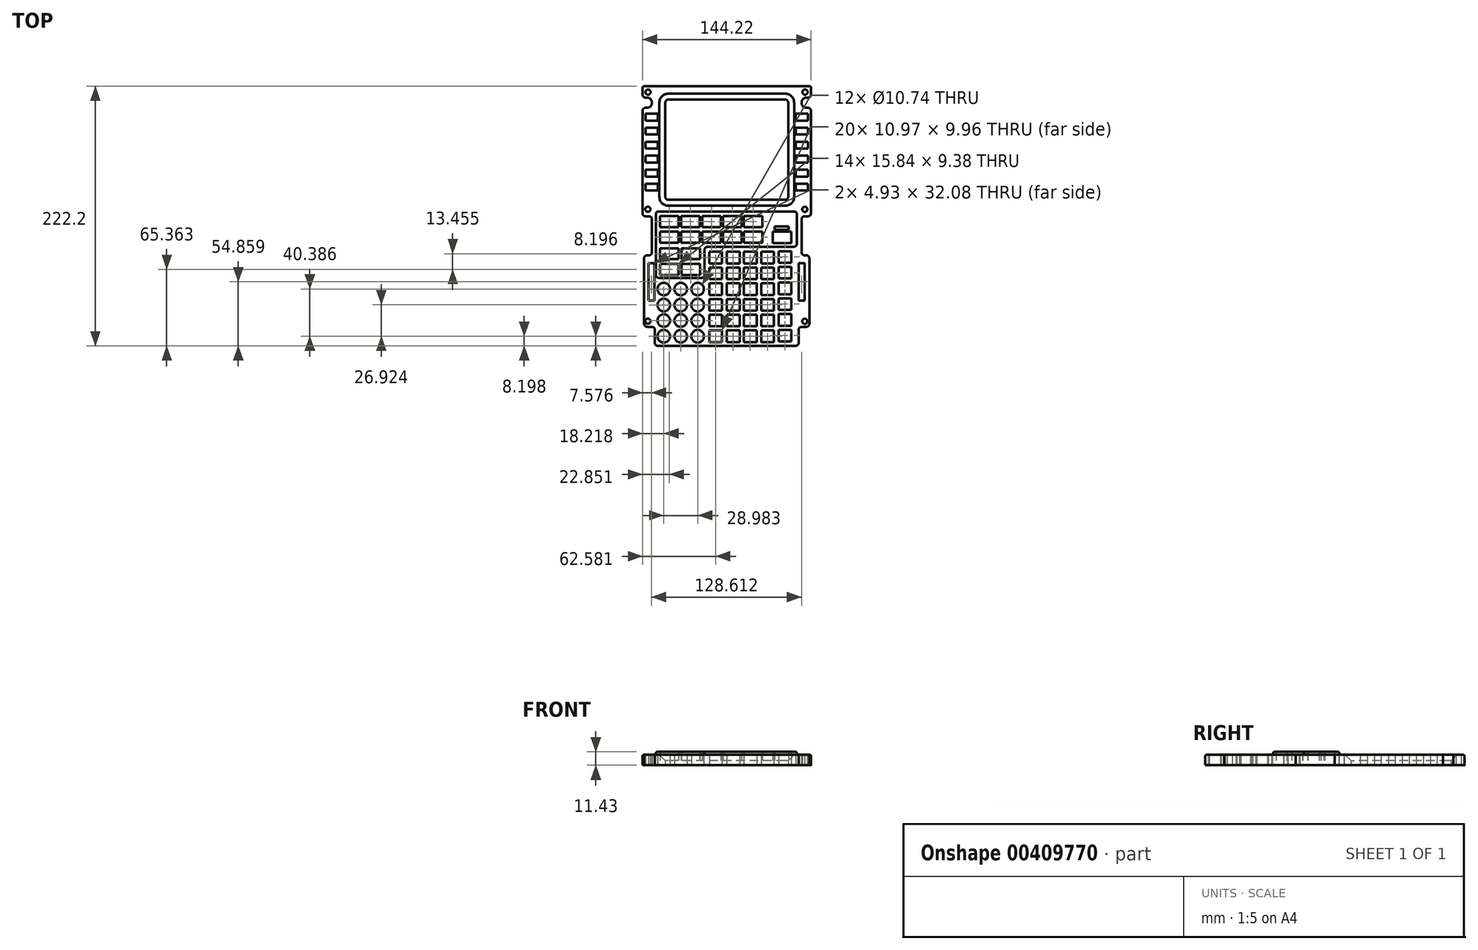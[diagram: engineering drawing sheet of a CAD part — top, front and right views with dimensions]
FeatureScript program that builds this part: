
annotation { "Feature Type Name" : "Feature", "Feature Type Description" : "" }
export const myFeature = defineFeature(function(context is Context, id is Id, definition is map)
    precondition{}
    {
        {
            var Q0;
            Q0=qCreatedBy(makeId("Top.planeOp"),FACE);
            var sketch = newSketch(context, id + "F0", { "sketchPlane" : qUnion([Q0])});
            skLineSegment(sketch, "E0.bottom", {"start": v(73.07, 113.67) * mm, "end": v(-73.07, 113.67) * mm});
            skLineSegment(sketch, "E0.top", {"start": v(73.07, -113.66) * mm, "end": v(-73.07, -113.66) * mm});
            skLineSegment(sketch, "E0.left", {"start": v(73.07, 113.67) * mm, "end": v(73.07, -113.66) * mm});
            skLineSegment(sketch, "E0.right", {"start": v(-73.07, 113.67) * mm, "end": v(-73.07, -113.66) * mm});
            skPoint(sketch, "E0.middle", {"position": v(0, 0) * mm});
            skLineSegment(sketch, "E1", {"start": v(0, 113.67) * mm, "end": v(0, 111.74) * mm});
            skLineSegment(sketch, "E2", {"start": v(-69.57, 102.01) * mm, "end": v(-68.34, 102.01) * mm});
            skLineSegment(sketch, "E3", {"start": v(-68.34, 93.24) * mm, "end": v(-69.57, 93.24) * mm});
            skLineSegment(sketch, "E4", {"start": v(-72.11, 90.7) * mm, "end": v(-72.11, 2.93) * mm});
            skLineSegment(sketch, "E5", {"start": v(-69.57, 0.4) * mm, "end": v(-66.53, 0.4) * mm});
            skLineSegment(sketch, "E6", {"start": v(-63.99, -2.15) * mm, "end": v(-63.99, -30.43) * mm});
            skLineSegment(sketch, "E7", {"start": v(-66.53, -32.97) * mm, "end": v(-68.15, -32.97) * mm});
            skLineSegment(sketch, "E8", {"start": v(-70.69, -35.51) * mm, "end": v(-70.69, -91.63) * mm});
            skLineSegment(sketch, "E9", {"start": v(-68.15, -94.17) * mm, "end": v(-64.1, -94.17) * mm});
            skLineSegment(sketch, "E10", {"start": v(-61.57, -96.71) * mm, "end": v(-61.57, -107.92) * mm});
            skLineSegment(sketch, "E11", {"start": v(-59.03, -110.46) * mm, "end": v(0, -110.46) * mm});
            skLineSegment(sketch, "E12", {"start": v(-72.11, 110.47) * mm, "end": v(-72.11, 108.94) * mm});
            skLineSegment(sketch, "E13", {"start": v(-70.84, 111.74) * mm, "end": v(-69.31, 111.74) * mm});
            skLineSegment(sketch, "E14", {"start": v(-72.11, 108.94) * mm, "end": v(-72.11, 104.55) * mm});
            skLineSegment(sketch, "E15", {"start": v(-69.31, 111.74) * mm, "end": v(0, 111.74) * mm});
            skPoint(sketch, "E16.visualSharp", {"position": v(-72.11, 111.74) * mm});
            skArc(sketch, "E16.filletArc", {"start": v(-70.84, 111.74) * mm, "mid": v(-71.74, 111.36) * mm, "end": v(-72.11, 110.47) * mm});
            skArc(sketch, "E17", {"start": v(-68.34, 93.24) * mm, "mid": v(-63.95, 97.62) * mm, "end": v(-68.34, 102.01) * mm});
            skPoint(sketch, "E18.visualSharp", {"position": v(-61.57, -110.46) * mm});
            skArc(sketch, "E18.filletArc", {"start": v(-61.57, -107.92) * mm, "mid": v(-60.82, -109.71) * mm, "end": v(-59.03, -110.46) * mm});
            skPoint(sketch, "E19.visualSharp", {"position": v(-61.57, -94.17) * mm});
            skArc(sketch, "E19.filletArc", {"start": v(-61.57, -96.71) * mm, "mid": v(-62.31, -94.92) * mm, "end": v(-64.1, -94.17) * mm});
            skPoint(sketch, "E20.visualSharp", {"position": v(-70.69, -94.17) * mm});
            skArc(sketch, "E20.filletArc", {"start": v(-70.69, -91.63) * mm, "mid": v(-69.94, -93.43) * mm, "end": v(-68.15, -94.17) * mm});
            skPoint(sketch, "E21.visualSharp", {"position": v(-70.69, -32.97) * mm});
            skArc(sketch, "E21.filletArc", {"start": v(-68.15, -32.97) * mm, "mid": v(-69.94, -33.72) * mm, "end": v(-70.69, -35.51) * mm});
            skPoint(sketch, "E22.visualSharp", {"position": v(-63.99, -32.97) * mm});
            skArc(sketch, "E22.filletArc", {"start": v(-66.53, -32.97) * mm, "mid": v(-64.73, -32.23) * mm, "end": v(-63.99, -30.43) * mm});
            skPoint(sketch, "E23.visualSharp", {"position": v(-63.99, 0.4) * mm});
            skArc(sketch, "E23.filletArc", {"start": v(-63.99, -2.15) * mm, "mid": v(-64.73, -0.35) * mm, "end": v(-66.53, 0.4) * mm});
            skPoint(sketch, "E24.visualSharp", {"position": v(-72.11, 0.4) * mm});
            skArc(sketch, "E24.filletArc", {"start": v(-72.11, 2.93) * mm, "mid": v(-71.37, 1.14) * mm, "end": v(-69.57, 0.4) * mm});
            skPoint(sketch, "E25.visualSharp", {"position": v(-72.11, 102.01) * mm});
            skArc(sketch, "E25.filletArc", {"start": v(-72.11, 104.55) * mm, "mid": v(-71.37, 102.76) * mm, "end": v(-69.57, 102.01) * mm});
            skPoint(sketch, "E26.visualSharp", {"position": v(-72.11, 93.24) * mm});
            skArc(sketch, "E26.filletArc", {"start": v(-69.57, 93.24) * mm, "mid": v(-71.37, 92.5) * mm, "end": v(-72.11, 90.7) * mm});
            skLineSegment(sketch, "E27.bottom", {"start": v(-59, 22.55) * mm, "end": v(-69.41, 22.55) * mm});
            skLineSegment(sketch, "E27.top", {"start": v(-59, 28.39) * mm, "end": v(-69.41, 28.39) * mm});
            skLineSegment(sketch, "E27.left", {"start": v(-59, 22.55) * mm, "end": v(-59, 28.39) * mm});
            skLineSegment(sketch, "E27.right", {"start": v(-69.41, 22.55) * mm, "end": v(-69.41, 28.39) * mm});
            skPoint(sketch, "E27.middle", {"position": v(-64.2, 25.47) * mm});
            skLineSegment(sketch, "E28.bottom", {"start": v(-59, 34.4) * mm, "end": v(-69.41, 34.4) * mm});
            skLineSegment(sketch, "E28.top", {"start": v(-59, 40.25) * mm, "end": v(-69.41, 40.25) * mm});
            skLineSegment(sketch, "E28.left", {"start": v(-59, 34.4) * mm, "end": v(-59, 40.25) * mm});
            skLineSegment(sketch, "E28.right", {"start": v(-69.41, 34.4) * mm, "end": v(-69.41, 40.25) * mm});
            skPoint(sketch, "E28.middle", {"position": v(-64.2, 37.33) * mm});
            skLineSegment(sketch, "E29.bottom", {"start": v(-59, 46.4) * mm, "end": v(-69.41, 46.4) * mm});
            skLineSegment(sketch, "E29.top", {"start": v(-59, 52.23) * mm, "end": v(-69.41, 52.23) * mm});
            skLineSegment(sketch, "E29.left", {"start": v(-59, 46.4) * mm, "end": v(-59, 52.23) * mm});
            skLineSegment(sketch, "E29.right", {"start": v(-69.41, 46.4) * mm, "end": v(-69.41, 52.23) * mm});
            skPoint(sketch, "E29.middle", {"position": v(-64.2, 49.31) * mm});
            skLineSegment(sketch, "E30.bottom", {"start": v(-59, 58.39) * mm, "end": v(-69.42, 58.39) * mm});
            skLineSegment(sketch, "E30.top", {"start": v(-59, 64.26) * mm, "end": v(-69.42, 64.26) * mm});
            skLineSegment(sketch, "E30.left", {"start": v(-59, 58.39) * mm, "end": v(-59, 64.26) * mm});
            skLineSegment(sketch, "E30.right", {"start": v(-69.42, 58.39) * mm, "end": v(-69.42, 64.26) * mm});
            skPoint(sketch, "E30.middle", {"position": v(-64.2, 61.32) * mm});
            skLineSegment(sketch, "E31.bottom", {"start": v(-59, 70.4) * mm, "end": v(-69.42, 70.4) * mm});
            skLineSegment(sketch, "E31.top", {"start": v(-59, 76.26) * mm, "end": v(-69.42, 76.26) * mm});
            skLineSegment(sketch, "E31.left", {"start": v(-59, 70.4) * mm, "end": v(-59, 76.26) * mm});
            skLineSegment(sketch, "E31.right", {"start": v(-69.42, 70.4) * mm, "end": v(-69.42, 76.26) * mm});
            skPoint(sketch, "E31.middle", {"position": v(-64.2, 73.33) * mm});
            skLineSegment(sketch, "E32.bottom", {"start": v(-59, 82.37) * mm, "end": v(-69.42, 82.37) * mm});
            skLineSegment(sketch, "E32.top", {"start": v(-59, 88.2) * mm, "end": v(-69.42, 88.2) * mm});
            skLineSegment(sketch, "E32.left", {"start": v(-59, 82.37) * mm, "end": v(-59, 88.2) * mm});
            skLineSegment(sketch, "E32.right", {"start": v(-69.42, 82.37) * mm, "end": v(-69.42, 88.2) * mm});
            skPoint(sketch, "E32.middle", {"position": v(-64.2, 85.29) * mm});
            skLineSegment(sketch, "E33", {"start": v(0, 100.27) * mm, "end": v(-50.04, 100.27) * mm});
            skLineSegment(sketch, "E34", {"start": v(-52.58, 97.73) * mm, "end": v(-52.58, 17.05) * mm});
            skLineSegment(sketch, "E35", {"start": v(-50.04, 14.51) * mm, "end": v(0, 14.51) * mm});
            skPoint(sketch, "E36.visualSharp", {"position": v(-52.58, 14.51) * mm});
            skArc(sketch, "E36.filletArc", {"start": v(-52.58, 17.05) * mm, "mid": v(-51.83, 15.26) * mm, "end": v(-50.04, 14.51) * mm});
            skPoint(sketch, "E37.visualSharp", {"position": v(-52.58, 100.27) * mm});
            skArc(sketch, "E37.filletArc", {"start": v(-50.04, 100.27) * mm, "mid": v(-51.83, 99.53) * mm, "end": v(-52.58, 97.73) * mm});
            skLineSegment(sketch, "E38", {"start": v(0, 105.03) * mm, "end": v(-54.96, 105.03) * mm});
            skLineSegment(sketch, "E39", {"start": v(-57.5, 102.49) * mm, "end": v(-57.5, 11.14) * mm});
            skLineSegment(sketch, "E40", {"start": v(-54.96, 8.6) * mm, "end": v(0, 8.6) * mm});
            skLineSegment(sketch, "E41.MirrorCS", {"start": v(59.03, -110.46) * mm, "end": v(0, -110.46) * mm});
            skArc(sketch, "E42.MirrorCS", {"start": v(61.57, -107.92) * mm, "mid": v(60.82, -109.71) * mm, "end": v(59.03, -110.46) * mm});
            skLineSegment(sketch, "E43.MirrorCS", {"start": v(61.57, -96.71) * mm, "end": v(61.57, -107.92) * mm});
            skArc(sketch, "E44.MirrorCS", {"start": v(61.57, -96.71) * mm, "mid": v(62.31, -94.92) * mm, "end": v(64.1, -94.17) * mm});
            skLineSegment(sketch, "E45.MirrorCS", {"start": v(68.15, -94.17) * mm, "end": v(64.1, -94.17) * mm});
            skArc(sketch, "E46.MirrorCS", {"start": v(70.69, -91.63) * mm, "mid": v(69.94, -93.43) * mm, "end": v(68.15, -94.17) * mm});
            skLineSegment(sketch, "E47.MirrorCS", {"start": v(70.69, -35.51) * mm, "end": v(70.69, -91.63) * mm});
            skArc(sketch, "E48.MirrorCS", {"start": v(68.15, -32.97) * mm, "mid": v(69.94, -33.72) * mm, "end": v(70.69, -35.51) * mm});
            skLineSegment(sketch, "E49.MirrorCS", {"start": v(66.53, -32.97) * mm, "end": v(68.15, -32.97) * mm});
            skArc(sketch, "E50.MirrorCS", {"start": v(66.53, -32.97) * mm, "mid": v(64.73, -32.23) * mm, "end": v(63.99, -30.43) * mm});
            skLineSegment(sketch, "E51.MirrorCS", {"start": v(63.99, -2.15) * mm, "end": v(63.99, -30.43) * mm});
            skArc(sketch, "E52.MirrorCS", {"start": v(63.99, -2.15) * mm, "mid": v(64.73, -0.35) * mm, "end": v(66.53, 0.4) * mm});
            skLineSegment(sketch, "E53.MirrorCS", {"start": v(69.57, 0.4) * mm, "end": v(66.53, 0.4) * mm});
            skArc(sketch, "E54.MirrorCS", {"start": v(72.11, 2.93) * mm, "mid": v(71.37, 1.14) * mm, "end": v(69.57, 0.4) * mm});
            skLineSegment(sketch, "E55.MirrorCS", {"start": v(72.11, 90.7) * mm, "end": v(72.11, 2.93) * mm});
            skLineSegment(sketch, "E56.MirrorCS", {"start": v(69.41, 22.55) * mm, "end": v(69.41, 28.39) * mm});
            skLineSegment(sketch, "E57.MirrorCS", {"start": v(59, 22.55) * mm, "end": v(69.41, 22.55) * mm});
            skLineSegment(sketch, "E58.MirrorCS", {"start": v(59, 22.55) * mm, "end": v(59, 28.39) * mm});
            skLineSegment(sketch, "E59.MirrorCS", {"start": v(59, 28.39) * mm, "end": v(69.41, 28.39) * mm});
            skLineSegment(sketch, "E60.MirrorCS", {"start": v(59, 34.4) * mm, "end": v(69.41, 34.4) * mm});
            skLineSegment(sketch, "E61.MirrorCS", {"start": v(59, 34.4) * mm, "end": v(59, 40.25) * mm});
            skLineSegment(sketch, "E62.MirrorCS", {"start": v(59, 40.25) * mm, "end": v(69.41, 40.25) * mm});
            skLineSegment(sketch, "E63.MirrorCS", {"start": v(69.41, 34.4) * mm, "end": v(69.41, 40.25) * mm});
            skLineSegment(sketch, "E64.MirrorCS", {"start": v(59, 46.4) * mm, "end": v(69.41, 46.4) * mm});
            skLineSegment(sketch, "E65.MirrorCS", {"start": v(59, 46.4) * mm, "end": v(59, 52.23) * mm});
            skLineSegment(sketch, "E66.MirrorCS", {"start": v(59, 52.23) * mm, "end": v(69.41, 52.23) * mm});
            skLineSegment(sketch, "E67.MirrorCS", {"start": v(69.41, 46.4) * mm, "end": v(69.41, 52.23) * mm});
            skLineSegment(sketch, "E68.MirrorCS", {"start": v(59, 58.39) * mm, "end": v(69.42, 58.39) * mm});
            skLineSegment(sketch, "E69.MirrorCS", {"start": v(69.42, 58.39) * mm, "end": v(69.42, 64.26) * mm});
            skLineSegment(sketch, "E70.MirrorCS", {"start": v(59, 64.26) * mm, "end": v(69.42, 64.26) * mm});
            skLineSegment(sketch, "E71.MirrorCS", {"start": v(59, 58.39) * mm, "end": v(59, 64.26) * mm});
            skLineSegment(sketch, "E72.MirrorCS", {"start": v(59, 70.4) * mm, "end": v(69.42, 70.4) * mm});
            skLineSegment(sketch, "E73.MirrorCS", {"start": v(69.42, 70.4) * mm, "end": v(69.42, 76.26) * mm});
            skLineSegment(sketch, "E74.MirrorCS", {"start": v(59, 76.26) * mm, "end": v(69.42, 76.26) * mm});
            skLineSegment(sketch, "E75.MirrorCS", {"start": v(59, 70.4) * mm, "end": v(59, 76.26) * mm});
            skLineSegment(sketch, "E76.MirrorCS", {"start": v(59, 82.37) * mm, "end": v(69.42, 82.37) * mm});
            skLineSegment(sketch, "E77.MirrorCS", {"start": v(69.42, 82.37) * mm, "end": v(69.42, 88.2) * mm});
            skLineSegment(sketch, "E78.MirrorCS", {"start": v(59, 88.2) * mm, "end": v(69.42, 88.2) * mm});
            skLineSegment(sketch, "E79.MirrorCS", {"start": v(59, 82.37) * mm, "end": v(59, 88.2) * mm});
            skArc(sketch, "E80.MirrorCS", {"start": v(69.57, 93.24) * mm, "mid": v(71.37, 92.5) * mm, "end": v(72.11, 90.7) * mm});
            skLineSegment(sketch, "E81.MirrorCS", {"start": v(68.34, 93.24) * mm, "end": v(69.57, 93.24) * mm});
            skArc(sketch, "E82.MirrorCS", {"start": v(68.34, 93.24) * mm, "mid": v(63.95, 97.62) * mm, "end": v(68.34, 102.01) * mm});
            skLineSegment(sketch, "E83.MirrorCS", {"start": v(69.57, 102.01) * mm, "end": v(68.34, 102.01) * mm});
            skArc(sketch, "E84.MirrorCS", {"start": v(72.11, 104.55) * mm, "mid": v(71.37, 102.76) * mm, "end": v(69.57, 102.01) * mm});
            skLineSegment(sketch, "E85.MirrorCS", {"start": v(72.11, 108.94) * mm, "end": v(72.11, 104.55) * mm});
            skLineSegment(sketch, "E86.MirrorCS", {"start": v(72.11, 110.47) * mm, "end": v(72.11, 108.94) * mm});
            skArc(sketch, "E87.MirrorCS", {"start": v(70.84, 111.74) * mm, "mid": v(71.74, 111.36) * mm, "end": v(72.11, 110.47) * mm});
            skLineSegment(sketch, "E88.MirrorCS", {"start": v(70.84, 111.74) * mm, "end": v(69.31, 111.74) * mm});
            skLineSegment(sketch, "E89.MirrorCS", {"start": v(69.31, 111.74) * mm, "end": v(0, 111.74) * mm});
            skLineSegment(sketch, "E90.MirrorCS", {"start": v(50.04, 14.51) * mm, "end": v(0, 14.51) * mm});
            skArc(sketch, "E91.MirrorCS", {"start": v(52.58, 17.05) * mm, "mid": v(51.83, 15.26) * mm, "end": v(50.04, 14.51) * mm});
            skLineSegment(sketch, "E92.MirrorCS", {"start": v(52.58, 97.73) * mm, "end": v(52.58, 17.05) * mm});
            skArc(sketch, "E93.MirrorCS", {"start": v(50.04, 100.27) * mm, "mid": v(51.83, 99.53) * mm, "end": v(52.58, 97.73) * mm});
            skLineSegment(sketch, "E94.MirrorCS", {"start": v(0, 100.27) * mm, "end": v(50.04, 100.27) * mm});
            skPoint(sketch, "E95.visualSharp", {"position": v(-57.5, 105.03) * mm});
            skArc(sketch, "E95.filletArc", {"start": v(-54.96, 105.03) * mm, "mid": v(-56.76, 104.28) * mm, "end": v(-57.5, 102.49) * mm});
            skPoint(sketch, "E96.visualSharp", {"position": v(-57.5, 8.6) * mm});
            skArc(sketch, "E96.filletArc", {"start": v(-57.5, 11.14) * mm, "mid": v(-56.76, 9.35) * mm, "end": v(-54.96, 8.6) * mm});
            skLineSegment(sketch, "E97.MirrorCS", {"start": v(54.96, 8.6) * mm, "end": v(0, 8.6) * mm});
            skArc(sketch, "E98.MirrorCS", {"start": v(57.5, 11.14) * mm, "mid": v(56.76, 9.35) * mm, "end": v(54.96, 8.6) * mm});
            skLineSegment(sketch, "E99.MirrorCS", {"start": v(57.5, 102.49) * mm, "end": v(57.5, 11.14) * mm});
            skArc(sketch, "E100.MirrorCS", {"start": v(54.96, 105.03) * mm, "mid": v(56.76, 104.28) * mm, "end": v(57.5, 102.49) * mm});
            skLineSegment(sketch, "E101.MirrorCS", {"start": v(0, 105.03) * mm, "end": v(54.96, 105.03) * mm});
            skCircle(sketch, "E102", {"center": v(-53.9, -61.88) * mm, "radius": 5.37 * mm});
            skCircle(sketch, "E103", {"center": v(-39.39, -61.88) * mm, "radius": 5.37 * mm});
            skCircle(sketch, "E104", {"center": v(-24.9, -61.88) * mm, "radius": 5.37 * mm});
            skCircle(sketch, "E105", {"center": v(-53.9, -75.58) * mm, "radius": 5.37 * mm});
            skCircle(sketch, "E106", {"center": v(-39.39, -75.58) * mm, "radius": 5.37 * mm});
            skCircle(sketch, "E107", {"center": v(-24.9, -75.58) * mm, "radius": 5.37 * mm});
            skCircle(sketch, "E108", {"center": v(-39.39, -88.8) * mm, "radius": 5.37 * mm});
            skCircle(sketch, "E109", {"center": v(-53.9, -88.8) * mm, "radius": 5.37 * mm});
            skCircle(sketch, "E110", {"center": v(-24.9, -88.8) * mm, "radius": 5.37 * mm});
            skCircle(sketch, "E111", {"center": v(-39.39, -102.26) * mm, "radius": 5.37 * mm});
            skCircle(sketch, "E112", {"center": v(-24.9, -102.26) * mm, "radius": 5.37 * mm});
            skCircle(sketch, "E113", {"center": v(-53.9, -102.26) * mm, "radius": 5.37 * mm});
            skLineSegment(sketch, "E114.bottom", {"start": v(-4.04, -29.98) * mm, "end": v(-15.02, -29.98) * mm});
            skLineSegment(sketch, "E114.top", {"start": v(-4.04, -39.93) * mm, "end": v(-15.02, -39.93) * mm});
            skLineSegment(sketch, "E114.left", {"start": v(-4.04, -29.98) * mm, "end": v(-4.04, -39.93) * mm});
            skLineSegment(sketch, "E114.right", {"start": v(-15.02, -29.98) * mm, "end": v(-15.02, -39.93) * mm});
            skPoint(sketch, "E114.middle", {"position": v(-9.53, -34.95) * mm});
            skLineSegment(sketch, "E115.bottom", {"start": v(-4.04, -43.44) * mm, "end": v(-15.02, -43.44) * mm});
            skLineSegment(sketch, "E115.top", {"start": v(-4.04, -53.4) * mm, "end": v(-15.02, -53.4) * mm});
            skLineSegment(sketch, "E115.left", {"start": v(-4.04, -43.44) * mm, "end": v(-4.04, -53.4) * mm});
            skLineSegment(sketch, "E115.right", {"start": v(-15.02, -43.44) * mm, "end": v(-15.02, -53.4) * mm});
            skPoint(sketch, "E115.middle", {"position": v(-9.53, -48.42) * mm});
            skLineSegment(sketch, "E116.bottom", {"start": v(-4.04, -66.85) * mm, "end": v(-15.02, -66.85) * mm});
            skLineSegment(sketch, "E116.top", {"start": v(-4.04, -56.9) * mm, "end": v(-15.02, -56.9) * mm});
            skLineSegment(sketch, "E116.left", {"start": v(-4.04, -66.85) * mm, "end": v(-4.04, -56.9) * mm});
            skLineSegment(sketch, "E116.right", {"start": v(-15.02, -66.85) * mm, "end": v(-15.02, -56.9) * mm});
            skPoint(sketch, "E116.middle", {"position": v(-9.53, -61.88) * mm});
            skLineSegment(sketch, "E117.bottom", {"start": v(-4.04, -80.32) * mm, "end": v(-15.02, -80.32) * mm});
            skLineSegment(sketch, "E117.top", {"start": v(-4.04, -70.36) * mm, "end": v(-15.02, -70.36) * mm});
            skLineSegment(sketch, "E117.left", {"start": v(-4.04, -80.32) * mm, "end": v(-4.04, -70.36) * mm});
            skLineSegment(sketch, "E117.right", {"start": v(-15.02, -80.32) * mm, "end": v(-15.02, -70.36) * mm});
            skPoint(sketch, "E117.middle", {"position": v(-9.53, -75.34) * mm});
            skLineSegment(sketch, "E118.bottom", {"start": v(-4.04, -93.79) * mm, "end": v(-15.02, -93.79) * mm});
            skLineSegment(sketch, "E118.top", {"start": v(-4.04, -83.82) * mm, "end": v(-15.02, -83.82) * mm});
            skLineSegment(sketch, "E118.left", {"start": v(-4.04, -93.79) * mm, "end": v(-4.04, -83.82) * mm});
            skLineSegment(sketch, "E118.right", {"start": v(-15.02, -93.79) * mm, "end": v(-15.02, -83.82) * mm});
            skPoint(sketch, "E118.middle", {"position": v(-9.53, -88.8) * mm});
            skLineSegment(sketch, "E119.bottom", {"start": v(-4.04, -97.28) * mm, "end": v(-15.02, -97.28) * mm});
            skLineSegment(sketch, "E119.top", {"start": v(-4.04, -107.24) * mm, "end": v(-15.02, -107.24) * mm});
            skLineSegment(sketch, "E119.left", {"start": v(-4.04, -97.28) * mm, "end": v(-4.04, -107.24) * mm});
            skLineSegment(sketch, "E119.right", {"start": v(-15.02, -97.28) * mm, "end": v(-15.02, -107.24) * mm});
            skPoint(sketch, "E119.middle", {"position": v(-9.53, -102.26) * mm});
            skLineSegment(sketch, "E120.bottom", {"start": v(10.97, -29.98) * mm, "end": v(0, -29.98) * mm});
            skLineSegment(sketch, "E120.top", {"start": v(10.97, -39.93) * mm, "end": v(0, -39.93) * mm});
            skLineSegment(sketch, "E120.left", {"start": v(10.97, -29.98) * mm, "end": v(10.97, -39.93) * mm});
            skLineSegment(sketch, "E120.right", {"start": v(0, -29.98) * mm, "end": v(0, -39.93) * mm});
            skLineSegment(sketch, "E121.bottom", {"start": v(10.97, -43.44) * mm, "end": v(0, -43.44) * mm});
            skLineSegment(sketch, "E121.top", {"start": v(10.97, -53.4) * mm, "end": v(0, -53.4) * mm});
            skLineSegment(sketch, "E121.left", {"start": v(10.97, -43.44) * mm, "end": v(10.97, -53.4) * mm});
            skLineSegment(sketch, "E121.right", {"start": v(0, -43.44) * mm, "end": v(0, -53.4) * mm});
            skLineSegment(sketch, "E122.bottom", {"start": v(10.97, -66.85) * mm, "end": v(0, -66.85) * mm});
            skLineSegment(sketch, "E122.top", {"start": v(10.97, -56.9) * mm, "end": v(0, -56.9) * mm});
            skLineSegment(sketch, "E122.left", {"start": v(10.97, -66.85) * mm, "end": v(10.97, -56.9) * mm});
            skLineSegment(sketch, "E122.right", {"start": v(0, -66.85) * mm, "end": v(0, -56.9) * mm});
            skLineSegment(sketch, "E123.bottom", {"start": v(10.97, -80.32) * mm, "end": v(0, -80.32) * mm});
            skLineSegment(sketch, "E123.top", {"start": v(10.97, -70.36) * mm, "end": v(0, -70.36) * mm});
            skLineSegment(sketch, "E123.left", {"start": v(10.97, -80.32) * mm, "end": v(10.97, -70.36) * mm});
            skLineSegment(sketch, "E123.right", {"start": v(0, -80.32) * mm, "end": v(0, -70.36) * mm});
            skLineSegment(sketch, "E124.bottom", {"start": v(10.97, -93.79) * mm, "end": v(0, -93.79) * mm});
            skLineSegment(sketch, "E124.top", {"start": v(10.97, -83.82) * mm, "end": v(0, -83.82) * mm});
            skLineSegment(sketch, "E124.left", {"start": v(10.97, -93.79) * mm, "end": v(10.97, -83.82) * mm});
            skLineSegment(sketch, "E124.right", {"start": v(0, -93.79) * mm, "end": v(0, -83.82) * mm});
            skLineSegment(sketch, "E125.bottom", {"start": v(10.97, -97.28) * mm, "end": v(0, -97.28) * mm});
            skLineSegment(sketch, "E125.top", {"start": v(10.97, -107.24) * mm, "end": v(0, -107.24) * mm});
            skLineSegment(sketch, "E125.left", {"start": v(10.97, -97.28) * mm, "end": v(10.97, -107.24) * mm});
            skLineSegment(sketch, "E125.right", {"start": v(0, -97.28) * mm, "end": v(0, -107.24) * mm});
            skLineSegment(sketch, "E126.bottom", {"start": v(25.63, -29.98) * mm, "end": v(14.65, -29.98) * mm});
            skLineSegment(sketch, "E126.top", {"start": v(25.63, -39.93) * mm, "end": v(14.65, -39.93) * mm});
            skLineSegment(sketch, "E126.left", {"start": v(25.63, -29.98) * mm, "end": v(25.63, -39.93) * mm});
            skLineSegment(sketch, "E126.right", {"start": v(14.65, -29.98) * mm, "end": v(14.65, -39.93) * mm});
            skLineSegment(sketch, "E127.bottom", {"start": v(25.63, -43.44) * mm, "end": v(14.65, -43.44) * mm});
            skLineSegment(sketch, "E127.top", {"start": v(25.63, -53.4) * mm, "end": v(14.65, -53.4) * mm});
            skLineSegment(sketch, "E127.left", {"start": v(25.63, -43.44) * mm, "end": v(25.63, -53.4) * mm});
            skLineSegment(sketch, "E127.right", {"start": v(14.65, -43.44) * mm, "end": v(14.65, -53.4) * mm});
            skLineSegment(sketch, "E128.bottom", {"start": v(25.63, -66.85) * mm, "end": v(14.65, -66.85) * mm});
            skLineSegment(sketch, "E128.top", {"start": v(25.63, -56.9) * mm, "end": v(14.65, -56.9) * mm});
            skLineSegment(sketch, "E128.left", {"start": v(25.63, -66.85) * mm, "end": v(25.63, -56.9) * mm});
            skLineSegment(sketch, "E128.right", {"start": v(14.65, -66.85) * mm, "end": v(14.65, -56.9) * mm});
            skLineSegment(sketch, "E129.bottom", {"start": v(25.63, -80.32) * mm, "end": v(14.65, -80.32) * mm});
            skLineSegment(sketch, "E129.top", {"start": v(25.63, -70.36) * mm, "end": v(14.65, -70.36) * mm});
            skLineSegment(sketch, "E129.left", {"start": v(25.63, -80.32) * mm, "end": v(25.63, -70.36) * mm});
            skLineSegment(sketch, "E129.right", {"start": v(14.65, -80.32) * mm, "end": v(14.65, -70.36) * mm});
            skLineSegment(sketch, "E130.bottom", {"start": v(25.63, -93.79) * mm, "end": v(14.65, -93.79) * mm});
            skLineSegment(sketch, "E130.top", {"start": v(25.63, -83.82) * mm, "end": v(14.65, -83.82) * mm});
            skLineSegment(sketch, "E130.left", {"start": v(25.63, -93.79) * mm, "end": v(25.63, -83.82) * mm});
            skLineSegment(sketch, "E130.right", {"start": v(14.65, -93.79) * mm, "end": v(14.65, -83.82) * mm});
            skLineSegment(sketch, "E131.bottom", {"start": v(25.63, -97.28) * mm, "end": v(14.65, -97.28) * mm});
            skLineSegment(sketch, "E131.top", {"start": v(25.63, -107.24) * mm, "end": v(14.65, -107.24) * mm});
            skLineSegment(sketch, "E131.left", {"start": v(25.63, -97.28) * mm, "end": v(25.63, -107.24) * mm});
            skLineSegment(sketch, "E131.right", {"start": v(14.65, -97.28) * mm, "end": v(14.65, -107.24) * mm});
            skLineSegment(sketch, "E132.bottom", {"start": v(40.46, -29.98) * mm, "end": v(29.49, -29.98) * mm});
            skLineSegment(sketch, "E132.top", {"start": v(40.46, -39.93) * mm, "end": v(29.49, -39.93) * mm});
            skLineSegment(sketch, "E132.left", {"start": v(40.46, -29.98) * mm, "end": v(40.46, -39.93) * mm});
            skLineSegment(sketch, "E132.right", {"start": v(29.49, -29.98) * mm, "end": v(29.49, -39.93) * mm});
            skLineSegment(sketch, "E133.bottom", {"start": v(40.46, -43.44) * mm, "end": v(29.49, -43.44) * mm});
            skLineSegment(sketch, "E133.top", {"start": v(40.46, -53.4) * mm, "end": v(29.49, -53.4) * mm});
            skLineSegment(sketch, "E133.left", {"start": v(40.46, -43.44) * mm, "end": v(40.46, -53.4) * mm});
            skLineSegment(sketch, "E133.right", {"start": v(29.49, -43.44) * mm, "end": v(29.49, -53.4) * mm});
            skLineSegment(sketch, "E134.bottom", {"start": v(40.46, -66.85) * mm, "end": v(29.49, -66.85) * mm});
            skLineSegment(sketch, "E134.top", {"start": v(40.46, -56.9) * mm, "end": v(29.49, -56.9) * mm});
            skLineSegment(sketch, "E134.left", {"start": v(40.46, -66.85) * mm, "end": v(40.46, -56.9) * mm});
            skLineSegment(sketch, "E134.right", {"start": v(29.49, -66.85) * mm, "end": v(29.49, -56.9) * mm});
            skLineSegment(sketch, "E135.bottom", {"start": v(40.46, -80.32) * mm, "end": v(29.49, -80.32) * mm});
            skLineSegment(sketch, "E135.top", {"start": v(40.46, -70.36) * mm, "end": v(29.49, -70.36) * mm});
            skLineSegment(sketch, "E135.left", {"start": v(40.46, -80.32) * mm, "end": v(40.46, -70.36) * mm});
            skLineSegment(sketch, "E135.right", {"start": v(29.49, -80.32) * mm, "end": v(29.49, -70.36) * mm});
            skLineSegment(sketch, "E136.bottom", {"start": v(40.46, -93.79) * mm, "end": v(29.49, -93.79) * mm});
            skLineSegment(sketch, "E136.top", {"start": v(40.46, -83.82) * mm, "end": v(29.49, -83.82) * mm});
            skLineSegment(sketch, "E136.left", {"start": v(40.46, -93.79) * mm, "end": v(40.46, -83.82) * mm});
            skLineSegment(sketch, "E136.right", {"start": v(29.49, -93.79) * mm, "end": v(29.49, -83.82) * mm});
            skLineSegment(sketch, "E137.bottom", {"start": v(40.46, -97.28) * mm, "end": v(29.49, -97.28) * mm});
            skLineSegment(sketch, "E137.top", {"start": v(40.46, -107.24) * mm, "end": v(29.49, -107.24) * mm});
            skLineSegment(sketch, "E137.left", {"start": v(40.46, -97.28) * mm, "end": v(40.46, -107.24) * mm});
            skLineSegment(sketch, "E137.right", {"start": v(29.49, -97.28) * mm, "end": v(29.49, -107.24) * mm});
            skLineSegment(sketch, "E138.bottom", {"start": v(55.3, -29.4) * mm, "end": v(44.32, -29.4) * mm});
            skLineSegment(sketch, "E138.top", {"start": v(55.3, -39.36) * mm, "end": v(44.32, -39.36) * mm});
            skLineSegment(sketch, "E138.left", {"start": v(55.3, -29.4) * mm, "end": v(55.3, -39.36) * mm});
            skLineSegment(sketch, "E138.right", {"start": v(44.32, -29.4) * mm, "end": v(44.32, -39.36) * mm});
            skLineSegment(sketch, "E139.bottom", {"start": v(55.3, -42.87) * mm, "end": v(44.32, -42.87) * mm});
            skLineSegment(sketch, "E139.top", {"start": v(55.3, -52.82) * mm, "end": v(44.32, -52.82) * mm});
            skLineSegment(sketch, "E139.left", {"start": v(55.3, -42.87) * mm, "end": v(55.3, -52.82) * mm});
            skLineSegment(sketch, "E139.right", {"start": v(44.32, -42.87) * mm, "end": v(44.32, -52.82) * mm});
            skLineSegment(sketch, "E140.bottom", {"start": v(55.3, -66.28) * mm, "end": v(44.32, -66.28) * mm});
            skLineSegment(sketch, "E140.top", {"start": v(55.3, -56.33) * mm, "end": v(44.32, -56.33) * mm});
            skLineSegment(sketch, "E140.left", {"start": v(55.3, -66.28) * mm, "end": v(55.3, -56.33) * mm});
            skLineSegment(sketch, "E140.right", {"start": v(44.32, -66.28) * mm, "end": v(44.32, -56.33) * mm});
            skLineSegment(sketch, "E141.bottom", {"start": v(55.3, -79.75) * mm, "end": v(44.32, -79.75) * mm});
            skLineSegment(sketch, "E141.top", {"start": v(55.3, -69.79) * mm, "end": v(44.32, -69.79) * mm});
            skLineSegment(sketch, "E141.left", {"start": v(55.3, -79.75) * mm, "end": v(55.3, -69.79) * mm});
            skLineSegment(sketch, "E141.right", {"start": v(44.32, -79.75) * mm, "end": v(44.32, -69.79) * mm});
            skLineSegment(sketch, "E142.bottom", {"start": v(55.3, -93.21) * mm, "end": v(44.32, -93.21) * mm});
            skLineSegment(sketch, "E142.top", {"start": v(55.3, -83.25) * mm, "end": v(44.32, -83.25) * mm});
            skLineSegment(sketch, "E142.left", {"start": v(55.3, -93.21) * mm, "end": v(55.3, -83.25) * mm});
            skLineSegment(sketch, "E142.right", {"start": v(44.32, -93.21) * mm, "end": v(44.32, -83.25) * mm});
            skLineSegment(sketch, "E143.bottom", {"start": v(55.3, -96.71) * mm, "end": v(44.32, -96.71) * mm});
            skLineSegment(sketch, "E143.top", {"start": v(55.3, -106.67) * mm, "end": v(44.32, -106.67) * mm});
            skLineSegment(sketch, "E143.left", {"start": v(55.3, -96.71) * mm, "end": v(55.3, -106.67) * mm});
            skLineSegment(sketch, "E143.right", {"start": v(44.32, -96.71) * mm, "end": v(44.32, -106.67) * mm});
            skLineSegment(sketch, "E144.bottom", {"start": v(61.61, -39.56) * mm, "end": v(66.54, -39.56) * mm});
            skLineSegment(sketch, "E144.top", {"start": v(61.61, -71.64) * mm, "end": v(66.54, -71.64) * mm});
            skLineSegment(sketch, "E144.left", {"start": v(61.61, -39.56) * mm, "end": v(61.61, -71.64) * mm});
            skLineSegment(sketch, "E144.right", {"start": v(66.54, -39.56) * mm, "end": v(66.54, -71.64) * mm});
            skLineSegment(sketch, "E145.bottom", {"start": v(-67, -39.56) * mm, "end": v(-62.07, -39.56) * mm});
            skLineSegment(sketch, "E145.top", {"start": v(-67, -71.64) * mm, "end": v(-62.07, -71.64) * mm});
            skLineSegment(sketch, "E145.left", {"start": v(-67, -39.56) * mm, "end": v(-67, -71.64) * mm});
            skLineSegment(sketch, "E145.right", {"start": v(-62.07, -39.56) * mm, "end": v(-62.07, -71.64) * mm});
            skLineSegment(sketch, "E146", {"start": v(-58.24, 4.59) * mm, "end": v(0, 4.59) * mm});
            skLineSegment(sketch, "E147", {"start": v(57.5, 4.59) * mm, "end": v(0, 4.59) * mm});
            skLineSegment(sketch, "E148", {"start": v(-60.78, -49.72) * mm, "end": v(-60.78, 2.05) * mm});
            skLineSegment(sketch, "E149", {"start": v(-21.53, -52.26) * mm, "end": v(-58.24, -52.26) * mm});
            skLineSegment(sketch, "E150", {"start": v(-19, -28.14) * mm, "end": v(-19, -49.72) * mm});
            skLineSegment(sketch, "E151", {"start": v(-16.45, -25.6) * mm, "end": v(57.5, -25.6) * mm});
            skLineSegment(sketch, "E152", {"start": v(60.04, -23.06) * mm, "end": v(60.04, 2.05) * mm});
            skPoint(sketch, "E153.visualSharp", {"position": v(60.04, 4.59) * mm});
            skArc(sketch, "E153.filletArc", {"start": v(60.04, 2.05) * mm, "mid": v(59.3, 3.85) * mm, "end": v(57.5, 4.59) * mm});
            skPoint(sketch, "E154.visualSharp", {"position": v(60.04, -25.6) * mm});
            skArc(sketch, "E154.filletArc", {"start": v(57.5, -25.6) * mm, "mid": v(59.3, -24.86) * mm, "end": v(60.04, -23.06) * mm});
            skPoint(sketch, "E155.visualSharp", {"position": v(-60.78, 4.59) * mm});
            skArc(sketch, "E155.filletArc", {"start": v(-58.24, 4.59) * mm, "mid": v(-60.03, 3.85) * mm, "end": v(-60.78, 2.05) * mm});
            skPoint(sketch, "E156.visualSharp", {"position": v(-60.78, -52.26) * mm});
            skArc(sketch, "E156.filletArc", {"start": v(-60.78, -49.72) * mm, "mid": v(-60.03, -51.52) * mm, "end": v(-58.24, -52.26) * mm});
            skPoint(sketch, "E157.visualSharp", {"position": v(-19, -52.26) * mm});
            skArc(sketch, "E157.filletArc", {"start": v(-21.53, -52.26) * mm, "mid": v(-19.74, -51.52) * mm, "end": v(-19, -49.72) * mm});
            skPoint(sketch, "E158.visualSharp", {"position": v(-19, -25.6) * mm});
            skArc(sketch, "E158.filletArc", {"start": v(-16.45, -25.6) * mm, "mid": v(-18.25, -26.35) * mm, "end": v(-19, -28.14) * mm});
            skLineSegment(sketch, "E159", {"start": v(-57.18, -8.79) * mm, "end": v(-57.18, 0.6) * mm});
            skLineSegment(sketch, "E160", {"start": v(-41.34, 0.6) * mm, "end": v(-57.18, 0.6) * mm});
            skLineSegment(sketch, "E161", {"start": v(-41.34, -8.79) * mm, "end": v(-57.18, -8.79) * mm});
            skLineSegment(sketch, "E162", {"start": v(-41.34, 0.6) * mm, "end": v(-41.34, -8.79) * mm});
            skLineSegment(sketch, "E163", {"start": v(-57.18, -22.24) * mm, "end": v(-57.18, -12.86) * mm});
            skLineSegment(sketch, "E164", {"start": v(-41.34, -12.86) * mm, "end": v(-57.18, -12.86) * mm});
            skLineSegment(sketch, "E165", {"start": v(-41.34, -22.24) * mm, "end": v(-57.18, -22.24) * mm});
            skLineSegment(sketch, "E166", {"start": v(-41.34, -12.86) * mm, "end": v(-41.34, -22.24) * mm});
            skLineSegment(sketch, "E167", {"start": v(-39.13, -8.79) * mm, "end": v(-39.13, 0.6) * mm});
            skLineSegment(sketch, "E168", {"start": v(-23.3, 0.6) * mm, "end": v(-39.13, 0.6) * mm});
            skLineSegment(sketch, "E169", {"start": v(-23.3, -8.79) * mm, "end": v(-39.13, -8.79) * mm});
            skLineSegment(sketch, "E170", {"start": v(-23.3, 0.6) * mm, "end": v(-23.3, -8.79) * mm});
            skLineSegment(sketch, "E171", {"start": v(-39.13, -22.24) * mm, "end": v(-39.13, -12.86) * mm});
            skLineSegment(sketch, "E172", {"start": v(-23.3, -12.86) * mm, "end": v(-39.13, -12.86) * mm});
            skLineSegment(sketch, "E173", {"start": v(-23.3, -22.24) * mm, "end": v(-39.13, -22.24) * mm});
            skLineSegment(sketch, "E174", {"start": v(-23.3, -12.86) * mm, "end": v(-23.3, -22.24) * mm});
            skLineSegment(sketch, "E175", {"start": v(-21.03, -8.79) * mm, "end": v(-21.03, 0.6) * mm});
            skLineSegment(sketch, "E176", {"start": v(-5.18, 0.6) * mm, "end": v(-21.03, 0.6) * mm});
            skLineSegment(sketch, "E177", {"start": v(-5.18, -8.79) * mm, "end": v(-21.03, -8.79) * mm});
            skLineSegment(sketch, "E178", {"start": v(-5.18, 0.6) * mm, "end": v(-5.18, -8.79) * mm});
            skLineSegment(sketch, "E179", {"start": v(-21.03, -22.24) * mm, "end": v(-21.03, -12.86) * mm});
            skLineSegment(sketch, "E180", {"start": v(-5.18, -12.86) * mm, "end": v(-21.03, -12.86) * mm});
            skLineSegment(sketch, "E181", {"start": v(-5.18, -22.24) * mm, "end": v(-21.03, -22.24) * mm});
            skLineSegment(sketch, "E182", {"start": v(-5.18, -12.86) * mm, "end": v(-5.18, -22.24) * mm});
            skLineSegment(sketch, "E183", {"start": v(-3.15, -8.79) * mm, "end": v(-3.15, 0.6) * mm});
            skLineSegment(sketch, "E184", {"start": v(12.69, 0.6) * mm, "end": v(-3.15, 0.6) * mm});
            skLineSegment(sketch, "E185", {"start": v(12.69, -8.79) * mm, "end": v(-3.15, -8.79) * mm});
            skLineSegment(sketch, "E186", {"start": v(12.69, 0.6) * mm, "end": v(12.69, -8.79) * mm});
            skLineSegment(sketch, "E187", {"start": v(-3.15, -22.24) * mm, "end": v(-3.15, -12.86) * mm});
            skLineSegment(sketch, "E188", {"start": v(12.69, -12.86) * mm, "end": v(-3.15, -12.86) * mm});
            skLineSegment(sketch, "E189", {"start": v(12.69, -22.24) * mm, "end": v(-3.15, -22.24) * mm});
            skLineSegment(sketch, "E190", {"start": v(12.69, -12.86) * mm, "end": v(12.69, -22.24) * mm});
            skLineSegment(sketch, "E191", {"start": v(14.65, -8.79) * mm, "end": v(14.65, 0.6) * mm});
            skLineSegment(sketch, "E192", {"start": v(30.5, 0.6) * mm, "end": v(14.65, 0.6) * mm});
            skLineSegment(sketch, "E193", {"start": v(30.5, -8.79) * mm, "end": v(14.65, -8.79) * mm});
            skLineSegment(sketch, "E194", {"start": v(30.5, 0.6) * mm, "end": v(30.5, -8.79) * mm});
            skLineSegment(sketch, "E195", {"start": v(14.65, -22.24) * mm, "end": v(14.65, -12.86) * mm});
            skLineSegment(sketch, "E196", {"start": v(30.5, -12.86) * mm, "end": v(14.65, -12.86) * mm});
            skLineSegment(sketch, "E197", {"start": v(30.5, -22.24) * mm, "end": v(14.65, -22.24) * mm});
            skLineSegment(sketch, "E198", {"start": v(30.5, -12.86) * mm, "end": v(30.5, -22.24) * mm});
            skLineSegment(sketch, "E199", {"start": v(-57.18, -36.33) * mm, "end": v(-57.18, -26.95) * mm});
            skLineSegment(sketch, "E200", {"start": v(-41.34, -26.95) * mm, "end": v(-57.18, -26.95) * mm});
            skLineSegment(sketch, "E201", {"start": v(-41.34, -36.33) * mm, "end": v(-57.18, -36.33) * mm});
            skLineSegment(sketch, "E202", {"start": v(-41.34, -26.95) * mm, "end": v(-41.34, -36.33) * mm});
            skLineSegment(sketch, "E203", {"start": v(-57.18, -49.79) * mm, "end": v(-57.18, -40.4) * mm});
            skLineSegment(sketch, "E204", {"start": v(-41.34, -40.4) * mm, "end": v(-57.18, -40.4) * mm});
            skLineSegment(sketch, "E205", {"start": v(-41.34, -49.79) * mm, "end": v(-57.18, -49.79) * mm});
            skLineSegment(sketch, "E206", {"start": v(-41.34, -40.4) * mm, "end": v(-41.34, -49.79) * mm});
            skLineSegment(sketch, "E207", {"start": v(-38.83, -36.27) * mm, "end": v(-38.83, -26.89) * mm});
            skLineSegment(sketch, "E208", {"start": v(-23, -26.89) * mm, "end": v(-38.83, -26.89) * mm});
            skLineSegment(sketch, "E209", {"start": v(-23, -36.27) * mm, "end": v(-38.83, -36.27) * mm});
            skLineSegment(sketch, "E210", {"start": v(-23, -26.89) * mm, "end": v(-23, -36.27) * mm});
            skLineSegment(sketch, "E211", {"start": v(-38.83, -49.72) * mm, "end": v(-38.83, -40.34) * mm});
            skLineSegment(sketch, "E212", {"start": v(-23, -40.34) * mm, "end": v(-38.83, -40.34) * mm});
            skLineSegment(sketch, "E213", {"start": v(-23, -49.72) * mm, "end": v(-38.83, -49.72) * mm});
            skLineSegment(sketch, "E214", {"start": v(-23, -40.34) * mm, "end": v(-23, -49.72) * mm});
            skLineSegment(sketch, "E215.bottom", {"start": v(39.23, -12.82) * mm, "end": v(55.26, -12.82) * mm});
            skLineSegment(sketch, "E215.top", {"start": v(39.23, -22.56) * mm, "end": v(55.26, -22.56) * mm});
            skLineSegment(sketch, "E215.left", {"start": v(39.23, -12.82) * mm, "end": v(39.23, -22.56) * mm});
            skLineSegment(sketch, "E215.right", {"start": v(55.26, -12.82) * mm, "end": v(55.26, -22.56) * mm});
            skLineSegment(sketch, "E216.bottom", {"start": v(40.96, -8.15) * mm, "end": v(52.9, -8.15) * mm});
            skLineSegment(sketch, "E216.top", {"start": v(40.96, -11.27) * mm, "end": v(52.9, -11.27) * mm});
            skLineSegment(sketch, "E216.left", {"start": v(40.96, -8.15) * mm, "end": v(40.96, -11.27) * mm});
            skLineSegment(sketch, "E216.right", {"start": v(52.9, -8.15) * mm, "end": v(52.9, -11.27) * mm});
            skCircle(sketch, "E217", {"center": v(-67.53, 6.45) * mm, "radius": 2.22 * mm});
            skCircle(sketch, "E218", {"center": v(-67.41, 106.64) * mm, "radius": 2.22 * mm});
            skCircle(sketch, "E219", {"center": v(67, 106.69) * mm, "radius": 2.22 * mm});
            skCircle(sketch, "E220", {"center": v(66.8, 6.35) * mm, "radius": 2.22 * mm});
            skCircle(sketch, "E221", {"center": v(66.82, -89.44) * mm, "radius": 2.23 * mm});
            skCircle(sketch, "E222", {"center": v(-67.53, -89.38) * mm, "radius": 2.22 * mm});
            skSolve(sketch);
        }
        {
            var Q0;
            Q0=makeQuery(id+"F0.imprint","IMPRINT",FACE,{"disambiguationData":[TD([[makeQuery(id+"F0.imprint","IMPRINT",EDGE,{"derivedFrom":sQuery(id+"F0.wireOp",EDGE,"E2")}),1.0]])]});
            extrude(context, id + "F1", {"entities" : qUnion([Q0]), "depth" : 8.9 * mm});
        }
        {
            var Q0;
            Q0=makeQuery(id+"F0.imprint","IMPRINT",FACE,{"disambiguationData":[TD([[makeQuery(id+"F0.imprint","IMPRINT",EDGE,{"derivedFrom":sQuery(id+"F0.wireOp",EDGE,"E146")}),-1.0]])]});
            extrude(context, id + "F2", {"entities" : qUnion([Q0]), "operationType" : NewBodyOperationType.ADD, "depth" : 11.43 * mm});
        }
        {
            var Q0;
            Q0=makeQuery(id+"F0.imprint","IMPRINT",FACE,{"disambiguationData":[TD([[makeQuery(id+"F0.imprint","IMPRINT",EDGE,{"derivedFrom":sQuery(id+"F0.wireOp",EDGE,"E33")}),-1.0]])]});
            extrude(context, id + "F3", {"entities" : qUnion([Q0]), "operationType" : NewBodyOperationType.ADD, "depth" : 8.9 * mm});
        }
        {
            var Q0;
            Q0=makeQuery(id+"F3.opExtrude","CAP_EDGE",EDGE,{"disambiguationData":[OSD([sQuery(id+"F0.wireOp",EDGE,"E34")])],"isStart":false});
            chamfer(context, id + "F4", {"entities" : qUnion([Q0]), "width" : 5.08 * mm, "tangentPropagation" : true});
        }
        {
            var Q0;
            Q0=makeQuery(id+"F2.opExtrude","CAP_EDGE",EDGE,{"disambiguationData":[OSD([sQuery(id+"F0.wireOp",EDGE,"E152")])],"isStart":false});
            fillet(context, id + "F5", {"entities" : qUnion([Q0]), "radius" : 1.27 * mm, "tangentPropagation" : true, "allowEdgeOverflow" : false});
        }
        {
            var Q0;
            Q0=makeQuery(id+"F1.opExtrude","CAP_EDGE",EDGE,{"disambiguationData":[OSD([sQuery(id+"F0.wireOp",EDGE,"E11"),sQuery(id+"F0.wireOp",EDGE,"E41.MirrorCS")])],"isStart":false});
            fillet(context, id + "F6", {"entities" : qUnion([Q0]), "radius" : 1.27 * mm, "tangentPropagation" : true, "allowEdgeOverflow" : false});
        }
    });
